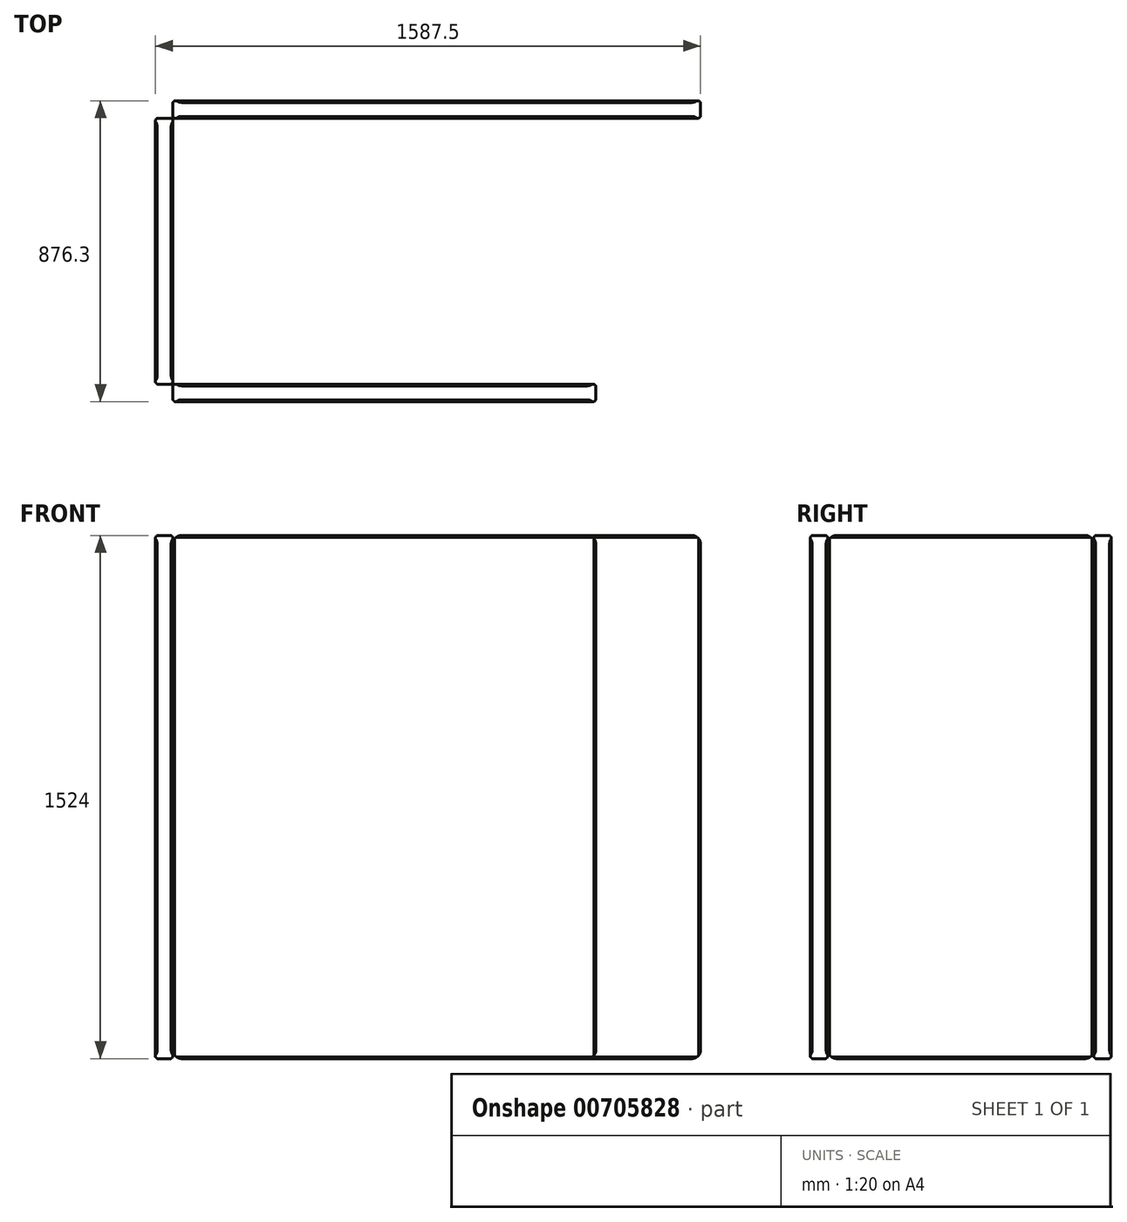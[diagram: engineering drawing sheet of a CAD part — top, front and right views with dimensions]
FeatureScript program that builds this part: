
annotation { "Feature Type Name" : "Feature", "Feature Type Description" : "" }
export const myFeature = defineFeature(function(context is Context, id is Id, definition is map)
    precondition{}
    {
        {
            var Q0;
            Q0=qCreatedBy(makeId("Top.planeOp"),FACE);
            var sketch = newSketch(context, id + "F0", { "sketchPlane" : qUnion([Q0])});
            skLineSegment(sketch, "E0.bottom", {"start": v(0, 0) * mm, "end": v(1231.9, 0) * mm});
            skLineSegment(sketch, "E0.top", {"start": v(0, 50.8) * mm, "end": v(1231.9, 50.8) * mm});
            skLineSegment(sketch, "E0.left", {"start": v(0, 0) * mm, "end": v(0, 50.8) * mm});
            skLineSegment(sketch, "E0.right", {"start": v(1231.9, 0) * mm, "end": v(1231.9, 50.8) * mm});
            skLineSegment(sketch, "E1.bottom", {"start": v(0, 50.8) * mm, "end": v(-50.8, 50.8) * mm});
            skLineSegment(sketch, "E1.top", {"start": v(0, 825.5) * mm, "end": v(-50.8, 825.5) * mm});
            skLineSegment(sketch, "E1.left", {"start": v(0, 50.8) * mm, "end": v(0, 825.5) * mm});
            skLineSegment(sketch, "E1.right", {"start": v(-50.8, 50.8) * mm, "end": v(-50.8, 825.5) * mm});
            skLineSegment(sketch, "E2.bottom", {"start": v(0, 825.5) * mm, "end": v(1536.7, 825.5) * mm});
            skLineSegment(sketch, "E2.top", {"start": v(0, 876.3) * mm, "end": v(1536.7, 876.3) * mm});
            skLineSegment(sketch, "E2.left", {"start": v(0, 825.5) * mm, "end": v(0, 876.3) * mm});
            skLineSegment(sketch, "E2.right", {"start": v(1536.7, 825.5) * mm, "end": v(1536.7, 876.3) * mm});
            skSolve(sketch);
        }
        {
            var Q0;
            Q0 = qSketchRegion(id + "F0", true);
            extrude(context, id + "F1", {"entities" : qUnion([Q0]), "depth" : 1524 * mm, "offsetDistance" : 25.4 * mm});
        }
        {
            var Q0;
            Q0=makeQuery(id+"F1.opExtrude","SWEPT_FACE",FACE,{"disambiguationData":[OSD([sQuery(id+"F0.wireOp",EDGE,"E0.bottom")])]});
            var Q1;
            Q1=makeQuery(id+"F1.opExtrude","SWEPT_FACE",FACE,{"disambiguationData":[OSD([sQuery(id+"F0.wireOp",EDGE,"E1.right")])]});
            var Q2;
            Q2=makeQuery(id+"F1.opExtrude","SWEPT_FACE",FACE,{"disambiguationData":[OSD([sQuery(id+"F0.wireOp",EDGE,"E1.left")])]});
            var Q3;
            Q3=makeQuery(id+"F1.opExtrude","SWEPT_FACE",FACE,{"disambiguationData":[OSD([sQuery(id+"F0.wireOp",EDGE,"E0.top")])]});
            var Q4;
            Q4=makeQuery(id+"F1.opExtrude","SWEPT_FACE",FACE,{"disambiguationData":[OSD([sQuery(id+"F0.wireOp",EDGE,"E2.bottom")])]});
            var Q5;
            Q5=makeQuery(id+"F1.opExtrude","SWEPT_FACE",FACE,{"disambiguationData":[OSD([sQuery(id+"F0.wireOp",EDGE,"E2.top")])]});
            chamfer(context, id + "F2", {"entities" : qUnion([Q0, Q1, Q2, Q3, Q4, Q5]), "width" : 5.08 * mm, "tangentPropagation" : true});
        }
        {
            var Q0;
            Q0=makeQuery(id+"F1.opExtrude","CAP_EDGE",EDGE,{"disambiguationData":[OSD([sQuery(id+"F0.wireOp",EDGE,"E0.right")])],"isStart":false});
            var Q1;
            Q1=makeQuery(id+"F1.opExtrude","CAP_EDGE",EDGE,{"disambiguationData":[OSD([sQuery(id+"F0.wireOp",EDGE,"E1.bottom")])],"isStart":false});
            var Q2;
            Q2=makeQuery(id+"F1.opExtrude","CAP_EDGE",EDGE,{"disambiguationData":[OSD([sQuery(id+"F0.wireOp",EDGE,"E0.left")])],"isStart":false});
            var Q3;
            Q3=makeQuery(id+"F1.opExtrude","CAP_EDGE",EDGE,{"disambiguationData":[OSD([sQuery(id+"F0.wireOp",EDGE,"E1.top")])],"isStart":false});
            var Q4;
            Q4=makeQuery(id+"F1.opExtrude","CAP_EDGE",EDGE,{"disambiguationData":[OSD([sQuery(id+"F0.wireOp",EDGE,"E0.right")])],"isStart":true});
            var Q5;
            Q5=makeQuery(id+"F1.opExtrude","CAP_EDGE",EDGE,{"disambiguationData":[OSD([sQuery(id+"F0.wireOp",EDGE,"E0.left")])],"isStart":true});
            var Q6;
            Q6=makeQuery(id+"F1.opExtrude","CAP_EDGE",EDGE,{"disambiguationData":[OSD([sQuery(id+"F0.wireOp",EDGE,"E1.bottom")])],"isStart":true});
            var Q7;
            Q7=makeQuery(id+"F1.opExtrude","CAP_EDGE",EDGE,{"disambiguationData":[OSD([sQuery(id+"F0.wireOp",EDGE,"E1.top")])],"isStart":true});
            var Q8;
            Q8=makeQuery(id+"F1.opExtrude","CAP_EDGE",EDGE,{"disambiguationData":[OSD([sQuery(id+"F0.wireOp",EDGE,"E2.left")])],"isStart":false});
            var Q9;
            Q9=makeQuery(id+"F1.opExtrude","CAP_EDGE",EDGE,{"disambiguationData":[OSD([sQuery(id+"F0.wireOp",EDGE,"E2.right")])],"isStart":false});
            var Q10;
            Q10=makeQuery(id+"F1.opExtrude","CAP_EDGE",EDGE,{"disambiguationData":[OSD([sQuery(id+"F0.wireOp",EDGE,"E2.left")])],"isStart":true});
            var Q11;
            Q11=makeQuery(id+"F1.opExtrude","CAP_EDGE",EDGE,{"disambiguationData":[OSD([sQuery(id+"F0.wireOp",EDGE,"E2.right")])],"isStart":true});
            fillet(context, id + "F3", {"entities" : qUnion([Q0, Q1, Q2, Q3, Q4, Q5, Q6, Q7, Q8, Q9, Q10, Q11]), "radius" : 25.4 * mm, "tangentPropagation" : true, "allowEdgeOverflow" : false});
        }
    });
